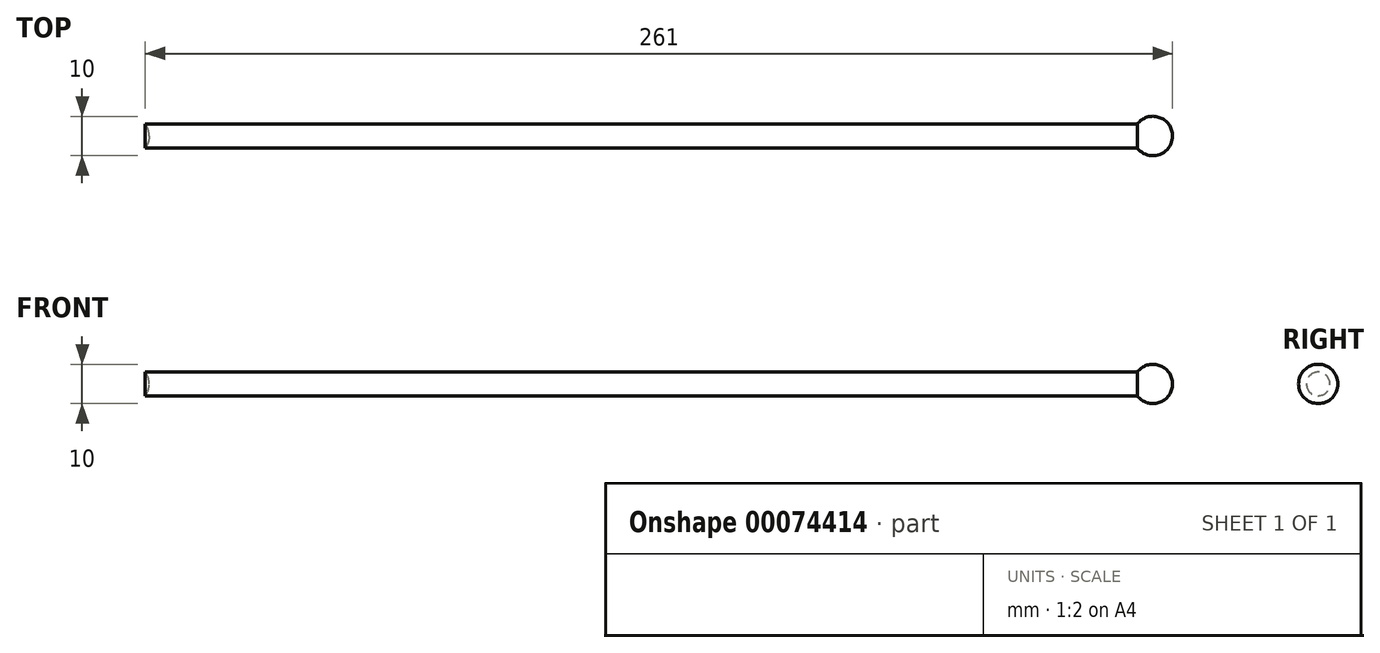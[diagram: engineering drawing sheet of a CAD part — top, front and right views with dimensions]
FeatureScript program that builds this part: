
annotation { "Feature Type Name" : "Feature", "Feature Type Description" : "" }
export const myFeature = defineFeature(function(context is Context, id is Id, definition is map)
    precondition{}
    {
        {
            var Q0;
            Q0=qCreatedBy(makeId("Top.planeOp"),FACE);
            var sketch = newSketch(context, id + "F0", { "sketchPlane" : qUnion([Q0])});
            skLineSegment(sketch, "E0", {"start": v(-50.25, 0) * mm, "end": v(219.75, 0) * mm});
            skArc(sketch, "E1", {"start": v(209.75, 0) * mm, "mid": v(214.75, -5) * mm, "end": v(219.75, 0) * mm});
            skArc(sketch, "E2", {"start": v(-50.25, 0) * mm, "mid": v(-45.25, -5) * mm, "end": v(-40.25, 0) * mm});
            skLineSegment(sketch, "E3", {"start": v(-41.25, -3) * mm, "end": v(210.75, -3) * mm});
            skSolve(sketch);
        }
        {
            var Q0;
            {var subQ0=sQuery(id+"F0.wireOp",EDGE,"E2");var subQ1=sQuery(id+"F0.wireOp",EDGE,"E0");var subQ2=makeQuery(id+"F0.imprint","INTERSECT",VERTEX,{"disambiguationData":[OD(0.0)],"derivedFrom":[subQ1,subQ0]});Q0=makeQuery(id+"F0.imprint","IMPRINT",FACE,{"disambiguationData":[TD([[makeQuery(id+"F0.imprint","IMPRINT",EDGE,{"disambiguationData":[TD([[subQ2,-1.0]])],"derivedFrom":subQ1}),-1.0]])]});}
            var Q1;
            {var subQ5=sQuery(id+"F0.wireOp",EDGE,"E3");Q1=makeQuery(id+"F0.imprint","IMPRINT",FACE,{"disambiguationData":[TD([[makeQuery(id+"F0.imprint","IMPRINT",EDGE,{"derivedFrom":subQ5}),1.0]])]});}
            var Q2;
            {var subQ0=sQuery(id+"F0.wireOp",EDGE,"E1");var subQ1=sQuery(id+"F0.wireOp",EDGE,"E0");var subQ2=makeQuery(id+"F0.imprint","INTERSECT",VERTEX,{"disambiguationData":[OD(0.0)],"derivedFrom":[subQ1,subQ0]});Q2=makeQuery(id+"F0.imprint","IMPRINT",FACE,{"disambiguationData":[TD([[makeQuery(id+"F0.imprint","IMPRINT",EDGE,{"disambiguationData":[TD([[subQ2,1.0]])],"derivedFrom":subQ1}),-1.0]])]});}
            var Q3;
            Q3=sQuery(id+"F0.wireOp",EDGE,"E0");
            revolve(context, id + "F1", {"entities" : qUnion([Q0, Q1, Q2]), "axis" : qUnion([Q3]), "revolveType" : RevolveType.FULL});
        }
    });
